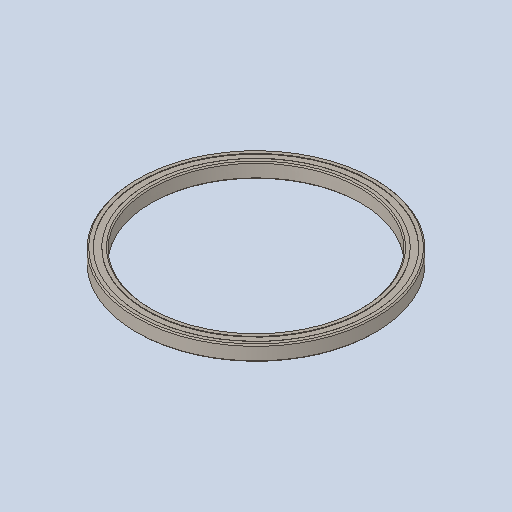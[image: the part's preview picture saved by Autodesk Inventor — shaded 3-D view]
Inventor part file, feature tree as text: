
AUTODESK INVENTOR PART (.ipt)
format: ipt  version: 2023 (Build 270158000, 158)  size: 126,464 bytes
history: native  units: in
note: dims shown in document units (in); Inventor stores cm internally (conversion verified against a paired STEP export)
features: revolve x1
ambient origin geometry x8: Origin, YZ Plane, XZ Plane, XY Plane, X Axis, Y Axis, Z Axis, Center Point
bodies: Solid1 (feature_tree)
feature tree (1):
  revolve  "Revolve1"  [1 undecoded]
note: 1 required parameter value undecoded (feature->parameter linkage not recoverable at this tier; creation-order binding heuristic only, values carry confidence <= 0.55)
